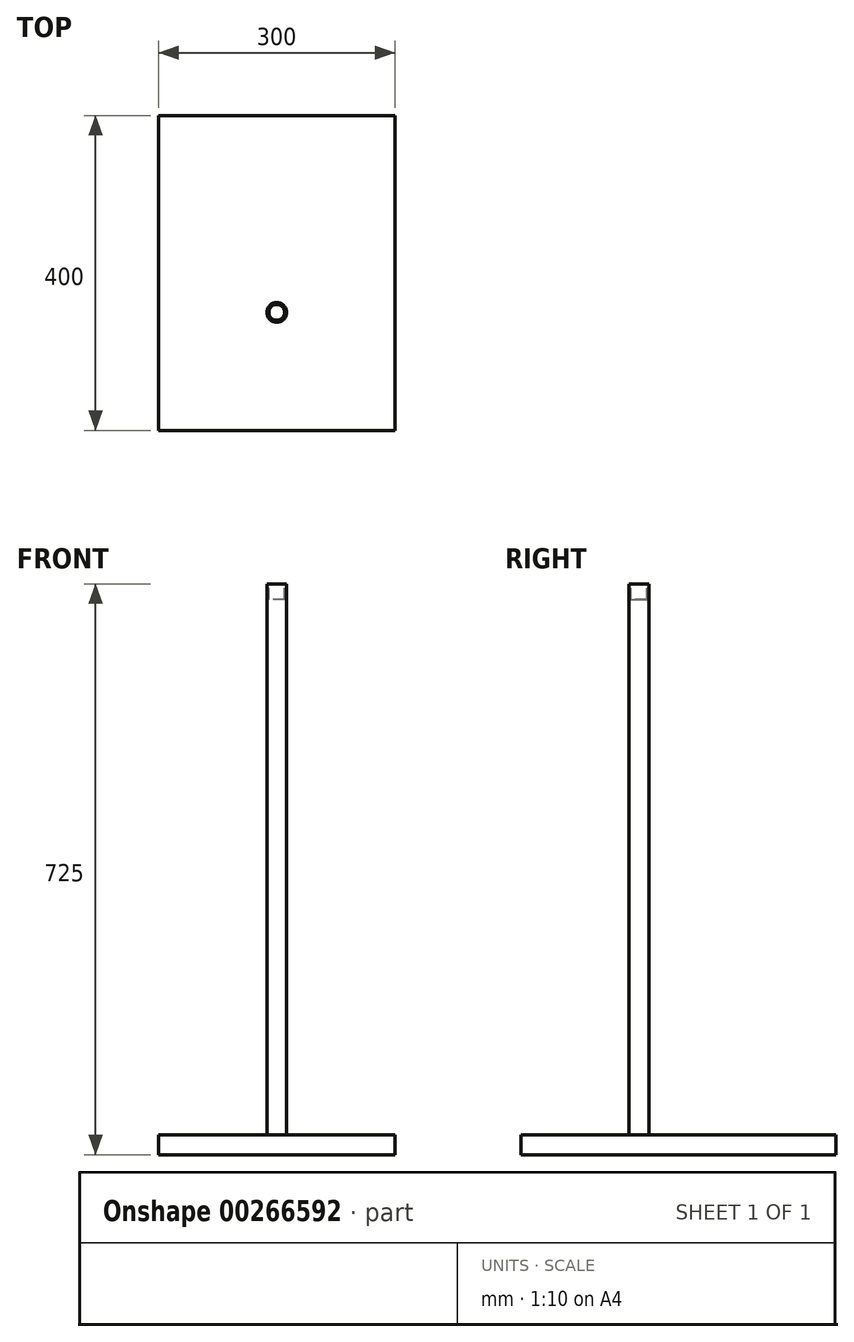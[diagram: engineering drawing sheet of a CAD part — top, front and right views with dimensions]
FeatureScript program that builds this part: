
annotation { "Feature Type Name" : "Feature", "Feature Type Description" : "" }
export const myFeature = defineFeature(function(context is Context, id is Id, definition is map)
    precondition{}
    {
        {
            var Q0;
            Q0=qCreatedBy(makeId("Top.planeOp"),FACE);
            var sketch = newSketch(context, id + "F0", { "sketchPlane" : qUnion([Q0])});
            skLineSegment(sketch, "E0.bottom", {"start": v(0, 0) * mm, "end": v(300, 0) * mm});
            skLineSegment(sketch, "E0.top", {"start": v(0, -400) * mm, "end": v(300, -400) * mm});
            skLineSegment(sketch, "E0.left", {"start": v(0, 0) * mm, "end": v(0, -400) * mm});
            skLineSegment(sketch, "E0.right", {"start": v(300, 0) * mm, "end": v(300, -400) * mm});
            skSolve(sketch);
        }
        {
            var Q0;
            Q0=makeQuery(id+"F0.imprint","IMPRINT",FACE,{"disambiguationData":[TD([[makeQuery(id+"F0.imprint","IMPRINT",EDGE,{"derivedFrom":sQuery(id+"F0.wireOp",EDGE,"E0.bottom")}),-1.0]])]});
            extrude(context, id + "F1", {"entities" : qUnion([Q0]), "depth" : 25 * mm});
        }
        {
            var Q0;
            Q0=makeQuery(id+"F1.opExtrude","CAP_FACE",FACE,{"disambiguationData":[OSD([sQuery(id+"F0.wireOp",EDGE,"E0.bottom"),sQuery(id+"F0.wireOp",EDGE,"E0.top"),sQuery(id+"F0.wireOp",EDGE,"E0.left"),sQuery(id+"F0.wireOp",EDGE,"E0.right")])],"isStart":false});
            var sketch = newSketch(context, id + "F2", { "sketchPlane" : qUnion([Q0])});
            skCircle(sketch, "E1", {"center": v(150, -250) * mm, "radius": 12.5 * mm});
            skPoint(sketch, "E1.centerSnap0", {"position": v(150, -400) * mm});
            skSolve(sketch);
        }
        {
            var Q0;
            Q0 = qSketchRegion(id + "F2", true);
            extrude(context, id + "F3", {"entities" : qUnion([Q0]), "operationType" : NewBodyOperationType.ADD, "depth" : 700 * mm});
        }
        {
            var Q0;
            Q0=makeQuery(id+"F3.opExtrude","CAP_FACE",FACE,{"disambiguationData":[OSD([sQuery(id+"F2.wireOp",EDGE,"E1")])],"isStart":false});
            var sketch = newSketch(context, id + "F4", { "sketchPlane" : qUnion([Q0])});
            skCircle(sketch, "E2", {"center": v(150, -250) * mm, "radius": 10 * mm});
            skSolve(sketch);
        }
        {
            var Q0;
            Q0 = qSketchRegion(id + "F4", true);
            extrude(context, id + "F5", {"entities" : qUnion([Q0]), "operationType" : NewBodyOperationType.REMOVE, "oppositeDirection" : true, "depth" : 20 * mm});
        }
    });
